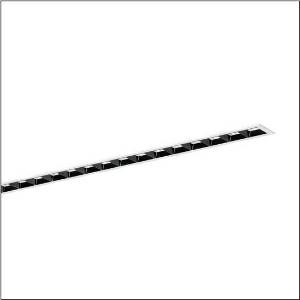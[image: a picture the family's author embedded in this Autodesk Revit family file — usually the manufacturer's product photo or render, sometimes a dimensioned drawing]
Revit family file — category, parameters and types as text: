
# Revit family: silica_r__21_51mx11db45wb_df67
name_source: partatom
category: Lighting Fixtures
units: mm (PartAtom-declared; Revit-internal decimal feet)

## family parameters
Cut with Voids When Loaded = No
Host = Face
Light Source = No
Part Type = Normal
Room Calculation Point = No
Round Connector Dimension = Use Diameter
Shared = No

## types (1)
- --- (1 x LED, 5400 lm, 32 W, 4000K)
    Apparent Load = 32 VA
    CIE Flux Codes = 87 99 100 100 100
    Color Rendering = 80
    Color Temperature = 4000K
    Default Elevation = 1800 mm
    Description = Silica® 21, office luminaire, primary light control with darklight reflector, of PMMA, black, CAT 2 (L<= 3000cd/m²), light emission: direct distribution, primary light characteristic: symmetric, installation type: recessed, LED, rated luminous flux: 5.400lm, luminous efficacy: 169lm/W, light colour: 840, colour temperature: 4000K, control gear: DALI 2, with terminal, 3+2-pole, max. 2.5mm², mains connection: 220..240V, AC, 50/60Hz, rated input power: 32W, luminaire housing, of aluminium, traffic white (RAL 9016), length: 1.528mm, width: 79mm, height: 53mm, protection rating (complete): IP20, insulation class (complete): insulation class I (protective earthing), certification: CE, ENEC, VDE, permissible operating ambient temperature: 0..+35°C, standard: EN 50419, packaging unit: 1 piece
    Height = 0 mm  [stored 0 ft]
    Lamp = 1 x LED
    Lamp Light Flux = 5400 lm
    Lamp Power = 32 W
    Lamp count = 1
    Length = 1527 mm
    Luminous efficacy = 169 lm/W
    Manufacturer = Siteco
    ModVariant = No
    Model = 51MX11DB45WB
    Mounting Place = Ceiling
    Mounting Type = Recessed
    Number of Poles = 1
    OnlyDefault = Yes
    Power Factor = 1
    Product Name = Silica® 21
    Product group = office luminaire | ceiling recessed
    ProductGroupID = 401
    Protection Class = Protection class I
    Protection Degree = IP 20
    RLX_Detail_Level = 1
    RLX_Emergency_Light_Flux = 0 lm
    RLX_Emergency_Type = 0
    RLX_Emergency_Type_DB = No
    RlxData = <blob elided: 42253 chars, md5=e60b6891>
    Socket = socket
    Standby Power = 0 W
    System Light Flux = 5400 lm
    System Power = 32 W
    Type Comments = factory setting: luminous flux: 100 % | dim-lin: 254 | 367 mA
    Type Image = l_1335880.jpg
    URL = http://relux.com
    VarID = @adj_123454
    Voltage = 0 V
    Weight = 0.00 kg
    Width = 79 mm

note: [stored X ft] marks values corroborated as IEEE doubles in the binary element streams (Revit-internal decimal feet)

## geometry (parser evidence)
native form markers: Blend x4, Sweep x9
no freeform markers — native parametric forms only
